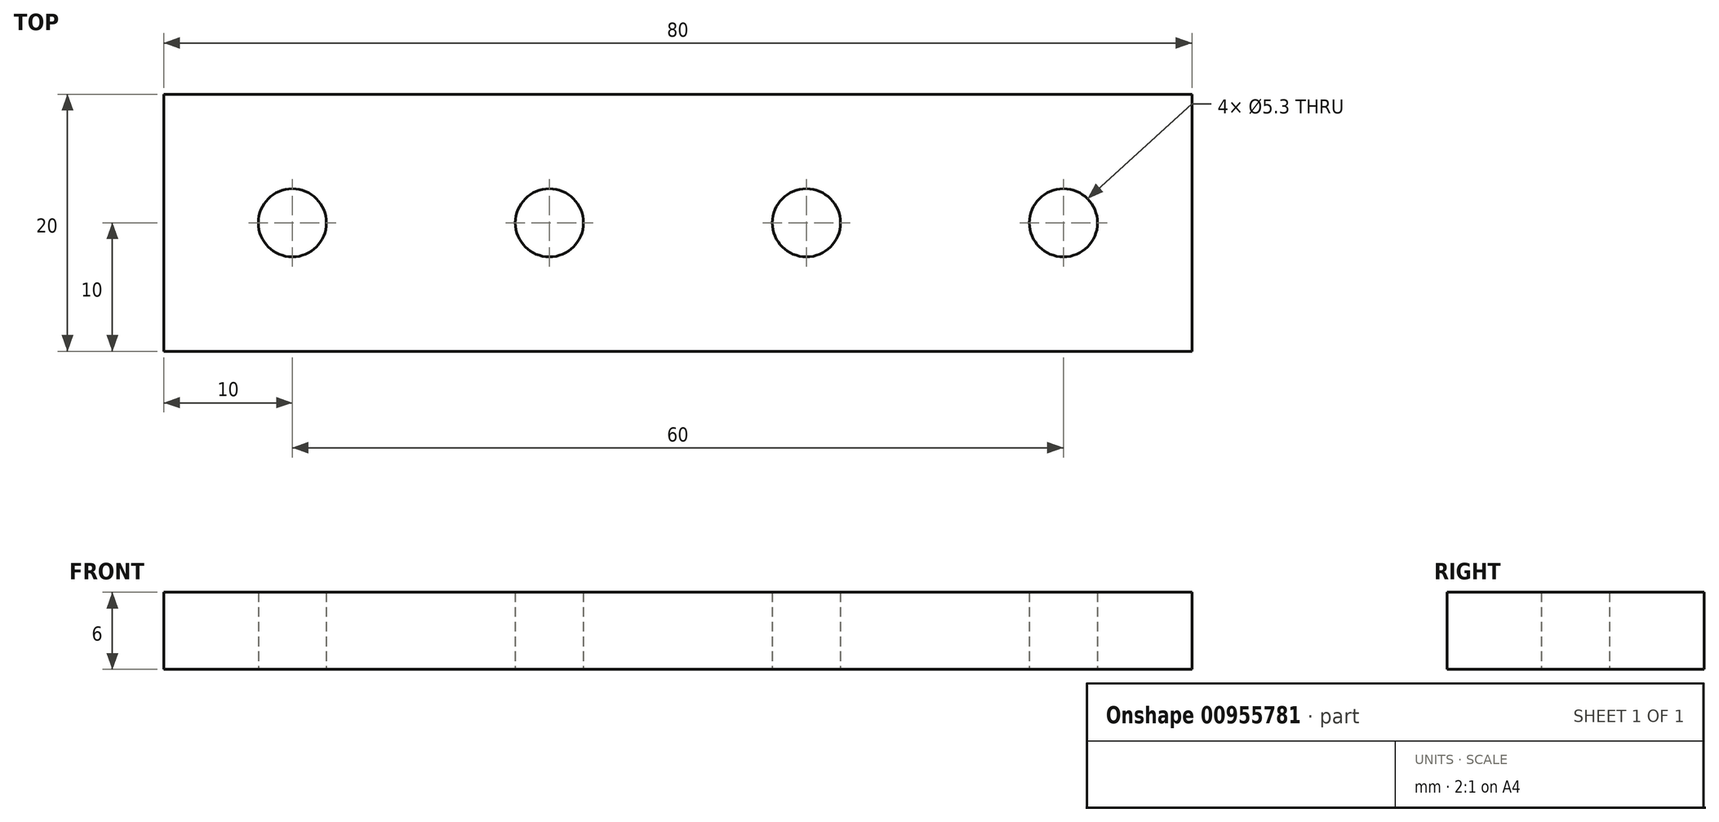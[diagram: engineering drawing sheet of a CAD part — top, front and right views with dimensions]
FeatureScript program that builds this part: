
annotation { "Feature Type Name" : "Feature", "Feature Type Description" : "" }
export const myFeature = defineFeature(function(context is Context, id is Id, definition is map)
    precondition{}
    {
        {
            var Q0;
            Q0=qCreatedBy(makeId("Top.planeOp"),FACE);
            var sketch = newSketch(context, id + "F0", { "sketchPlane" : qUnion([Q0])});
            skLineSegment(sketch, "E0.bottom", {"start": v(-40, -10) * mm, "end": v(40, -10) * mm});
            skLineSegment(sketch, "E0.top", {"start": v(-40, 10) * mm, "end": v(40, 10) * mm});
            skLineSegment(sketch, "E0.left", {"start": v(-40, -10) * mm, "end": v(-40, 10) * mm});
            skLineSegment(sketch, "E0.right", {"start": v(40, -10) * mm, "end": v(40, 10) * mm});
            skPoint(sketch, "E0.middle", {"position": v(0, 0) * mm});
            skCircle(sketch, "E1", {"center": v(-30, 0) * mm, "radius": 2.65 * mm});
            skCircle(sketch, "E2.1.0.0", {"center": v(-10, 0) * mm, "radius": 2.65 * mm});
            skCircle(sketch, "E2.2.0.0", {"center": v(10, 0) * mm, "radius": 2.65 * mm});
            skCircle(sketch, "E2.3.0.0", {"center": v(30, 0) * mm, "radius": 2.65 * mm});
            skLineSegment(sketch, "E2.direction1", {"start": v(-30, 0) * mm, "end": v(-10, 0) * mm, "construction": true});
            skSolve(sketch);
        }
        {
            var Q0;
            Q0=makeQuery(id+"F0.imprint","IMPRINT",FACE,{"disambiguationData":[TD([[makeQuery(id+"F0.imprint","IMPRINT",EDGE,{"derivedFrom":sQuery(id+"F0.wireOp",EDGE,"E0.bottom")}),1.0]])]});
            extrude(context, id + "F1", {"entities" : qUnion([Q0]), "depth" : 6 * mm, "offsetDistance" : 25 * mm});
        }
    });
